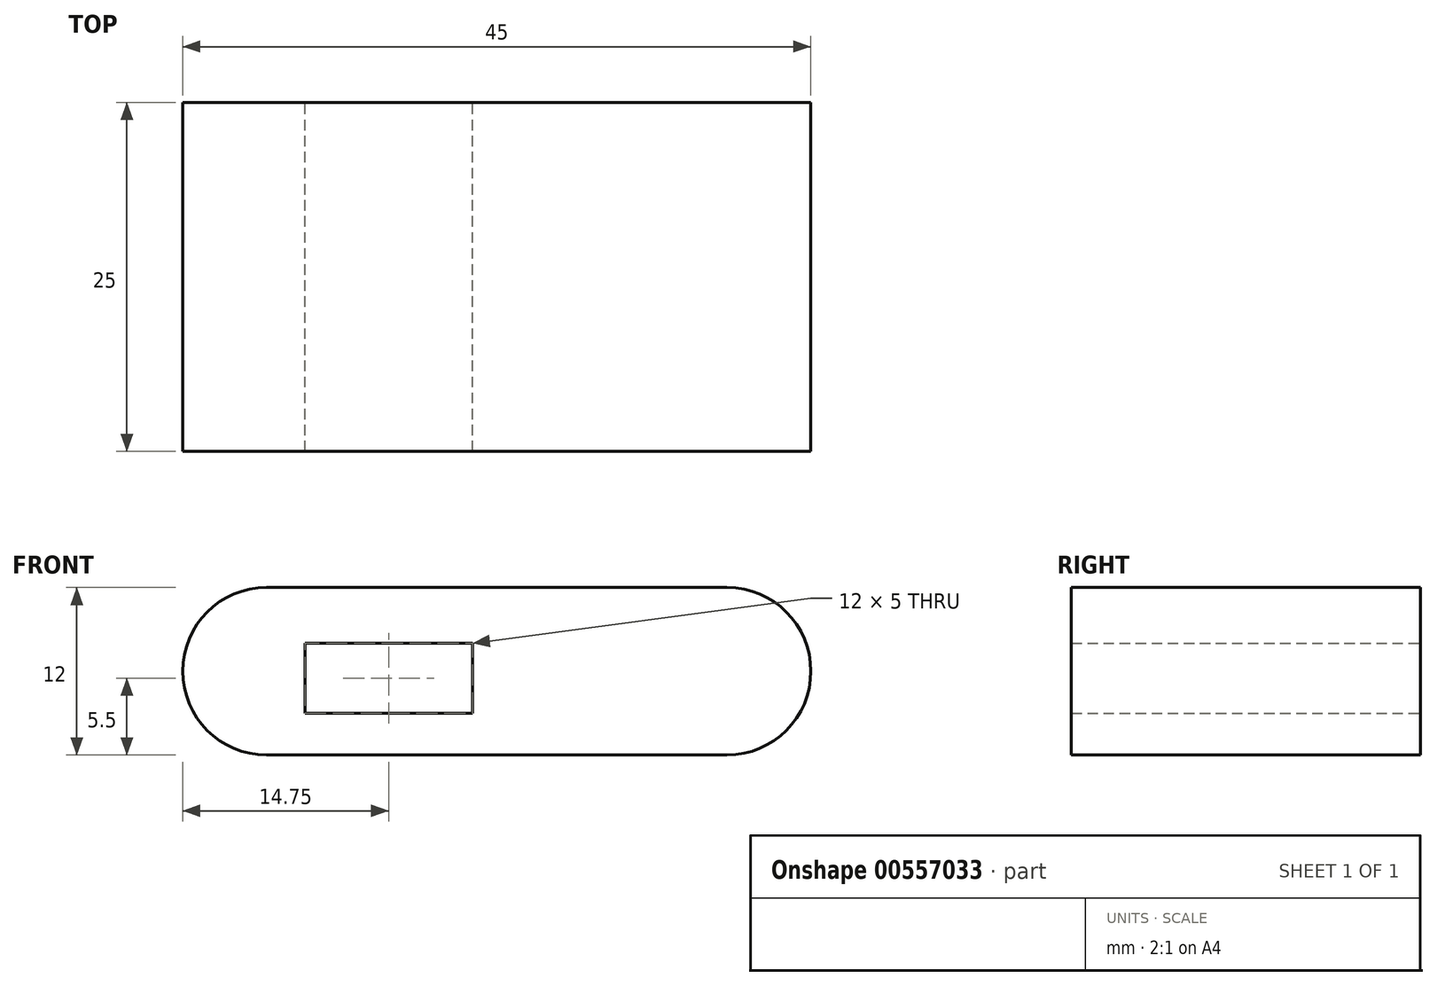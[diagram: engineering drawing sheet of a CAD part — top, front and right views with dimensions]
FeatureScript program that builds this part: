
annotation { "Feature Type Name" : "Feature", "Feature Type Description" : "" }
export const myFeature = defineFeature(function(context is Context, id is Id, definition is map)
    precondition{}
    {
        {
            var Q0;
            Q0=qCreatedBy(makeId("Front.planeOp"),FACE);
            var sketch = newSketch(context, id + "F0", { "sketchPlane" : qUnion([Q0])});
            skLineSegment(sketch, "E0.bottom", {"start": v(-12, 30.42) * mm, "end": v(0, 30.42) * mm});
            skLineSegment(sketch, "E0.top", {"start": v(-12, 25.42) * mm, "end": v(0, 25.42) * mm});
            skLineSegment(sketch, "E0.left", {"start": v(-12, 30.42) * mm, "end": v(-12, 25.42) * mm});
            skLineSegment(sketch, "E0.right", {"start": v(0, 30.42) * mm, "end": v(0, 25.42) * mm});
            skLineSegment(sketch, "E1.bottom", {"start": v(0, 6) * mm, "end": v(-16.5, 6) * mm});
            skLineSegment(sketch, "E1.top", {"start": v(0, -6) * mm, "end": v(-16.5, -6) * mm});
            skLineSegment(sketch, "E2.bottom", {"start": v(0, 6) * mm, "end": v(16.5, 6) * mm});
            skLineSegment(sketch, "E2.top", {"start": v(0, -6) * mm, "end": v(16.5, -6) * mm});
            skArc(sketch, "E3", {"start": v(-16.5, 6) * mm, "mid": v(-22.5, 0) * mm, "end": v(-16.5, -6) * mm});
            skArc(sketch, "E4", {"start": v(16.5, -6) * mm, "mid": v(22.5, 0) * mm, "end": v(16.5, 6) * mm});
            skLineSegment(sketch, "E5.bottom", {"start": v(-13.75, -3) * mm, "end": v(-1.75, -3) * mm});
            skLineSegment(sketch, "E5.top", {"start": v(-13.75, 2) * mm, "end": v(-1.75, 2) * mm});
            skLineSegment(sketch, "E5.left", {"start": v(-13.75, -3) * mm, "end": v(-13.75, 2) * mm});
            skLineSegment(sketch, "E5.right", {"start": v(-1.75, -3) * mm, "end": v(-1.75, 2) * mm});
            skSolve(sketch);
        }
        {
            var Q0;
            Q0=makeQuery(id+"F0.imprint","IMPRINT",FACE,{"disambiguationData":[TD([[makeQuery(id+"F0.imprint","IMPRINT",EDGE,{"derivedFrom":sQuery(id+"F0.wireOp",EDGE,"E1.bottom")}),1.0]])]});
            extrude(context, id + "F1", {"entities" : qUnion([Q0]), "depth" : 25 * mm, "offsetDistance" : 25 * mm});
        }
    });
